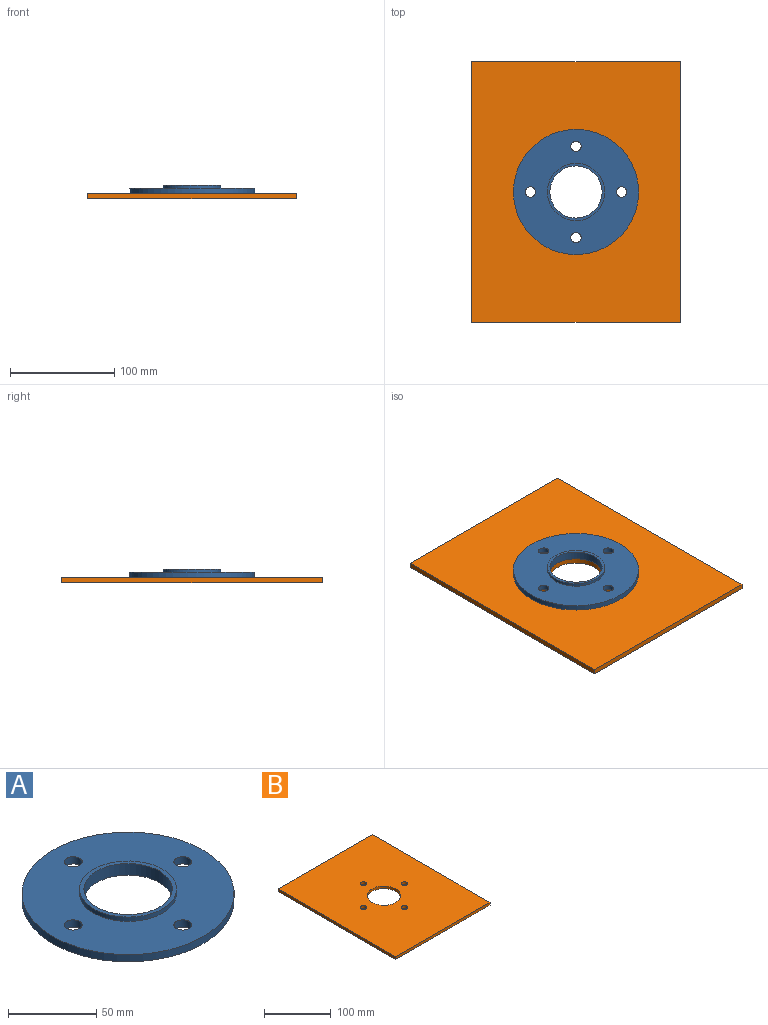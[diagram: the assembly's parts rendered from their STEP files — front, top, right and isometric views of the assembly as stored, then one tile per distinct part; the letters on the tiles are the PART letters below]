
ASSEMBLY  parts=2 mates=1
PART A: 10 faces, bbox 120x120x8 mm
  f0: cylinder r=25mm len=50mm, axis (0,0,-1), area 1256.6mm2, adj f2,f3
  f1: cylinder r=27.5mm len=55mm, axis (0,0,-1), area 518.4mm2, adj f2,f5
  f2: plane 55x55mm, normal (0,0,1), area 412.3mm2, adj f0,f1
  f3: plane 120x120mm, normal (0,0,-1), area 9032.1mm2, adj f0,f4,f6,f7,f8,f9
  f4: cylinder r=60mm len=120mm, axis (0,0,-1), area 1885mm2, adj f3,f5
  f5: plane 120x120mm, normal (0,0,1), area 8619.7mm2, adj f1,f4,f6,f7,f8,f9
  f6: cylinder r=5mm len=10mm, axis (0,0,-1), area 157.1mm2, adj f3,f5
  f7: cylinder r=5mm len=10mm, axis (0,0,-1), area 157.1mm2, adj f3,f5
  f8: cylinder r=5mm len=10mm, axis (0,0,-1), area 157.1mm2, adj f3,f5
  f9: cylinder r=5mm len=10mm, axis (0,0,-1), area 157.1mm2, adj f3,f5
PART B: 11 faces, bbox 200x250x5 mm
  f0: plane 250x5mm, normal (1,0,0), area 1250mm2, adj f1,f3,f5,f6
  f1: plane 200x5mm, normal (0,1,0), area 1000mm2, adj f0,f2,f5,f6
  f2: plane 250x5mm, normal (-1,0,0), area 1250mm2, adj f1,f3,f5,f6
  f3: plane 200x5mm, normal (0,-1,0), area 1000mm2, adj f0,f2,f5,f6
  f4: cylinder r=25mm len=50mm, axis (0,0,-1), area 785.4mm2, adj f5,f6
  f5: plane 250x200mm, normal (0,0,1), area 47722.3mm2, adj f0,f1,f2,f3,f4,f7,f8,f9
  f6: plane 250x200mm, normal (0,0,-1), area 47722.3mm2, adj f0,f1,f2,f3,f4,f7,f8,f9
  f7: cylinder r=5mm len=10mm, axis (0,0,-1), area 157.1mm2, adj f5,f6
  f8: cylinder r=5mm len=10mm, axis (0,0,-1), area 157.1mm2, adj f5,f6
  f9: cylinder r=5mm len=10mm, axis (0,0,-1), area 157.1mm2, adj f5,f6
  f10: cylinder r=5mm len=10mm, axis (0,0,-1), area 157.1mm2, adj f5,f6
PLACE A t=(-92.44,-45.25,38.29)mm
PLACE B t=(-92.44,-45.25,33.29)mm
MATE planar B.f4 <-> A.f4  axis (0,0,1) through (-92.44,-45.25,38.29)mm
